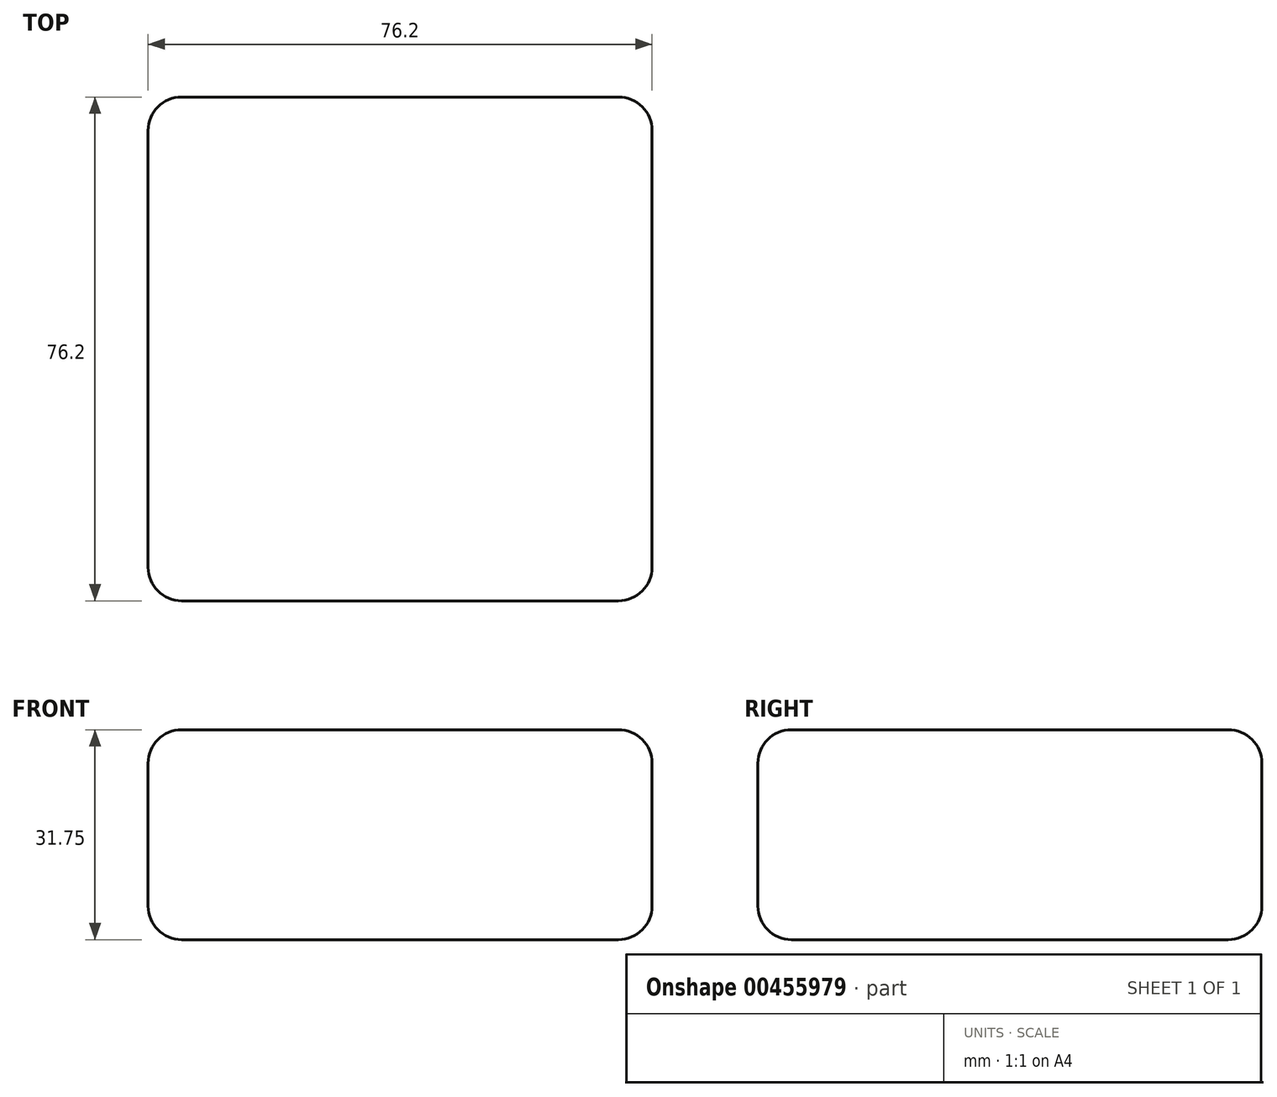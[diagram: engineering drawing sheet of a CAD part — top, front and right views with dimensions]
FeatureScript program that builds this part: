
annotation { "Feature Type Name" : "Feature", "Feature Type Description" : "" }
export const myFeature = defineFeature(function(context is Context, id is Id, definition is map)
    precondition{}
    {
        {
            var Q0;
            Q0=qCreatedBy(makeId("Top.planeOp"),FACE);
            var sketch = newSketch(context, id + "F0", { "sketchPlane" : qUnion([Q0])});
            skLineSegment(sketch, "E0.bottom", {"start": v(38.1, 38.1) * mm, "end": v(-38.1, 38.1) * mm});
            skLineSegment(sketch, "E0.top", {"start": v(38.1, -38.1) * mm, "end": v(-38.1, -38.1) * mm});
            skLineSegment(sketch, "E0.left", {"start": v(38.1, 38.1) * mm, "end": v(38.1, -38.1) * mm});
            skLineSegment(sketch, "E0.right", {"start": v(-38.1, 38.1) * mm, "end": v(-38.1, -38.1) * mm});
            skPoint(sketch, "E0.middle", {"position": v(0, 0) * mm});
            skSolve(sketch);
        }
        {
            var Q0;
            Q0=makeQuery(id+"F0.imprint","IMPRINT",FACE,{"disambiguationData":[TD([[makeQuery(id+"F0.imprint","IMPRINT",EDGE,{"derivedFrom":sQuery(id+"F0.wireOp",EDGE,"E0.bottom")}),1.0]])]});
            extrude(context, id + "F1", {"entities" : qUnion([Q0]), "oppositeDirection" : true, "depth" : 31.75 * mm});
        }
        {
            var Q0;
            Q0=makeQuery(id+"F1.opExtrude","CAP_EDGE",EDGE,{"disambiguationData":[OSD([sQuery(id+"F0.wireOp",EDGE,"E0.top")])],"isStart":true});
            var Q1;
            Q1=makeQuery(id+"F1.opExtrude","SWEPT_EDGE",EDGE,{"disambiguationData":[OSD([sQuery(id+"F0.wireOp",EDGE,"E0.top"),sQuery(id+"F0.wireOp",EDGE,"E0.left")])]});
            var Q2;
            Q2=makeQuery(id+"F1.opExtrude","CAP_EDGE",EDGE,{"disambiguationData":[OSD([sQuery(id+"F0.wireOp",EDGE,"E0.left")])],"isStart":true});
            var Q3;
            Q3=makeQuery(id+"F1.opExtrude","SWEPT_FACE",FACE,{"disambiguationData":[OSD([sQuery(id+"F0.wireOp",EDGE,"E0.left")])]});
            var Q4;
            Q4=makeQuery(id+"F1.opExtrude","CAP_EDGE",EDGE,{"disambiguationData":[OSD([sQuery(id+"F0.wireOp",EDGE,"E0.top")])],"isStart":false});
            var Q5;
            Q5=makeQuery(id+"F1.opExtrude","CAP_EDGE",EDGE,{"disambiguationData":[OSD([sQuery(id+"F0.wireOp",EDGE,"E0.right")])],"isStart":true});
            var Q6;
            Q6=makeQuery(id+"F1.opExtrude","CAP_EDGE",EDGE,{"disambiguationData":[OSD([sQuery(id+"F0.wireOp",EDGE,"E0.bottom")])],"isStart":true});
            fillet(context, id + "F2", {"entities" : qUnion([Q0, Q1, Q2, Q3, Q4, Q5, Q6]), "radius" : 5.08 * mm, "tangentPropagation" : true, "allowEdgeOverflow" : false});
        }
        {
            var Q0;
            Q0=makeQuery(id+"F1.opExtrude","CAP_EDGE",EDGE,{"disambiguationData":[OSD([sQuery(id+"F0.wireOp",EDGE,"E0.bottom")])],"isStart":false});
            var Q1;
            Q1=makeQuery(id+"F1.opExtrude","SWEPT_EDGE",EDGE,{"disambiguationData":[OSD([sQuery(id+"F0.wireOp",EDGE,"E0.bottom"),sQuery(id+"F0.wireOp",EDGE,"E0.right")])]});
            var Q2;
            Q2=makeQuery(id+"F1.opExtrude","CAP_EDGE",EDGE,{"disambiguationData":[OSD([sQuery(id+"F0.wireOp",EDGE,"E0.right")])],"isStart":false});
            var Q3;
            Q3=makeQuery(id+"F1.opExtrude","SWEPT_EDGE",EDGE,{"disambiguationData":[OSD([sQuery(id+"F0.wireOp",EDGE,"E0.top"),sQuery(id+"F0.wireOp",EDGE,"E0.right")])]});
            var Q4;
            {var subQ0=sQuery(id+"F0.wireOp",EDGE,"E0.top");Q4=makeQuery(id+"F2.opFillet","BLEND_EDGE",EDGE,{"blendedFrom":[makeQuery(id+"F1.opExtrude","CAP_EDGE",EDGE,{"disambiguationData":[OSD([subQ0])],"isStart":false}),makeQuery(id+"F1.opExtrude","CAP_FACE",FACE,{"disambiguationData":[OSD([sQuery(id+"F0.wireOp",EDGE,"E0.bottom"),subQ0,sQuery(id+"F0.wireOp",EDGE,"E0.left"),sQuery(id+"F0.wireOp",EDGE,"E0.right")])],"isStart":false})],"blendedInto":[makeQuery(id+"F1.opExtrude","CAP_FACE",FACE,{"disambiguationData":[OSD([sQuery(id+"F0.wireOp",EDGE,"E0.bottom"),subQ0,sQuery(id+"F0.wireOp",EDGE,"E0.left"),sQuery(id+"F0.wireOp",EDGE,"E0.right")])],"isStart":false})]});}
            fillet(context, id + "F3", {"entities" : qUnion([Q0, Q1, Q2, Q3, Q4]), "radius" : 5.08 * mm, "tangentPropagation" : true, "allowEdgeOverflow" : false});
        }
    });
